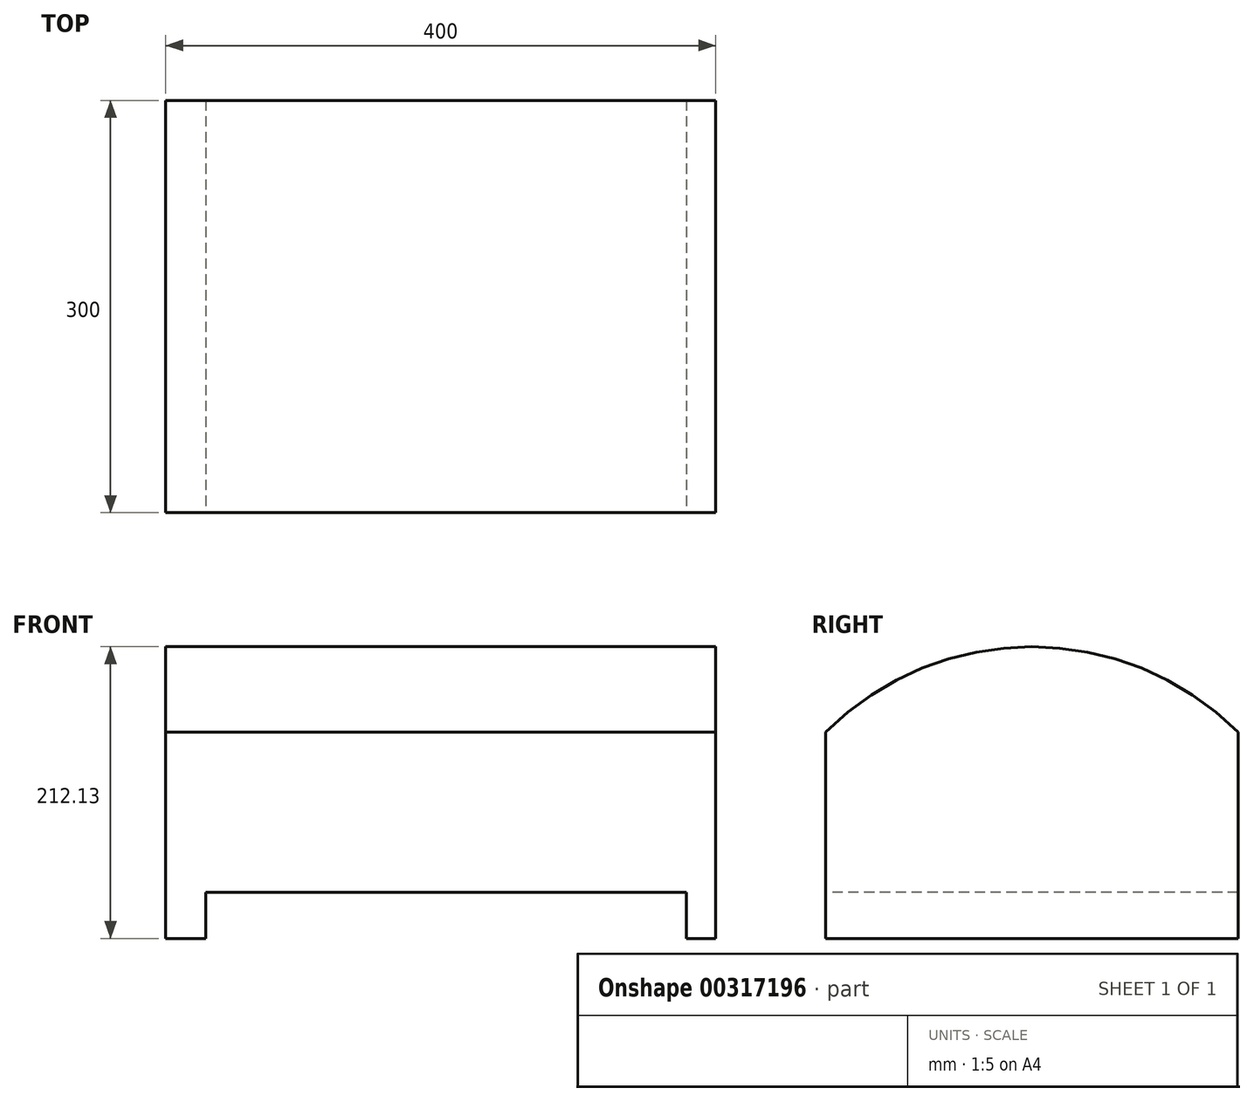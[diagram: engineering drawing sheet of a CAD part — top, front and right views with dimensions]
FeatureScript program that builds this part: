
annotation { "Feature Type Name" : "Feature", "Feature Type Description" : "" }
export const myFeature = defineFeature(function(context is Context, id is Id, definition is map)
    precondition{}
    {
        {
            var Q0;
            Q0=qCreatedBy(makeId("Right.planeOp"),FACE);
            var sketch = newSketch(context, id + "F0", { "sketchPlane" : qUnion([Q0])});
            skLineSegment(sketch, "E0.bottom", {"start": v(0, 0) * mm, "end": v(300, 0) * mm});
            skLineSegment(sketch, "E0.left", {"start": v(0, 0) * mm, "end": v(0, 150) * mm});
            skLineSegment(sketch, "E0.right", {"start": v(300, 0) * mm, "end": v(300, 150) * mm});
            skArc(sketch, "E1", {"start": v(300, 150) * mm, "mid": v(150, 212.13) * mm, "end": v(0, 150) * mm});
            skLineSegment(sketch, "E2", {"start": v(0, 150) * mm, "end": v(300, 150) * mm, "construction": true});
            skSolve(sketch);
        }
        {
            var Q0;
            Q0 = qSketchRegion(id + "F0", true);
            extrude(context, id + "F1", {"entities" : qUnion([Q0]), "depth" : 200 * mm, "hasSecondDirection" : true, "secondDirectionOppositeDirection" : true, "secondDirectionDepth" : 200 * mm});
        }
        {
            var Q0;
            Q0=makeQuery(id+"F1.opExtrude","SWEPT_FACE",FACE,{"disambiguationData":[OSD([sQuery(id+"F0.wireOp",EDGE,"E0.left")])]});
            var sketch = newSketch(context, id + "F2", { "sketchPlane" : qUnion([Q0])});
            skLineSegment(sketch, "E3.bottom", {"start": v(-170.74, 0) * mm, "end": v(178.87, 0) * mm});
            skLineSegment(sketch, "E3.top", {"start": v(-170.74, 33.6) * mm, "end": v(178.87, 33.6) * mm});
            skLineSegment(sketch, "E3.left", {"start": v(-170.74, 0) * mm, "end": v(-170.74, 33.6) * mm});
            skLineSegment(sketch, "E3.right", {"start": v(178.87, 0) * mm, "end": v(178.87, 33.6) * mm});
            skSolve(sketch);
        }
        {
            var Q0;
            Q0 = qSketchRegion(id + "F2", true);
            extrude(context, id + "F3", {"entities" : qUnion([Q0]), "operationType" : NewBodyOperationType.REMOVE, "oppositeDirection" : true, "depth" : 400 * mm});
        }
    });
